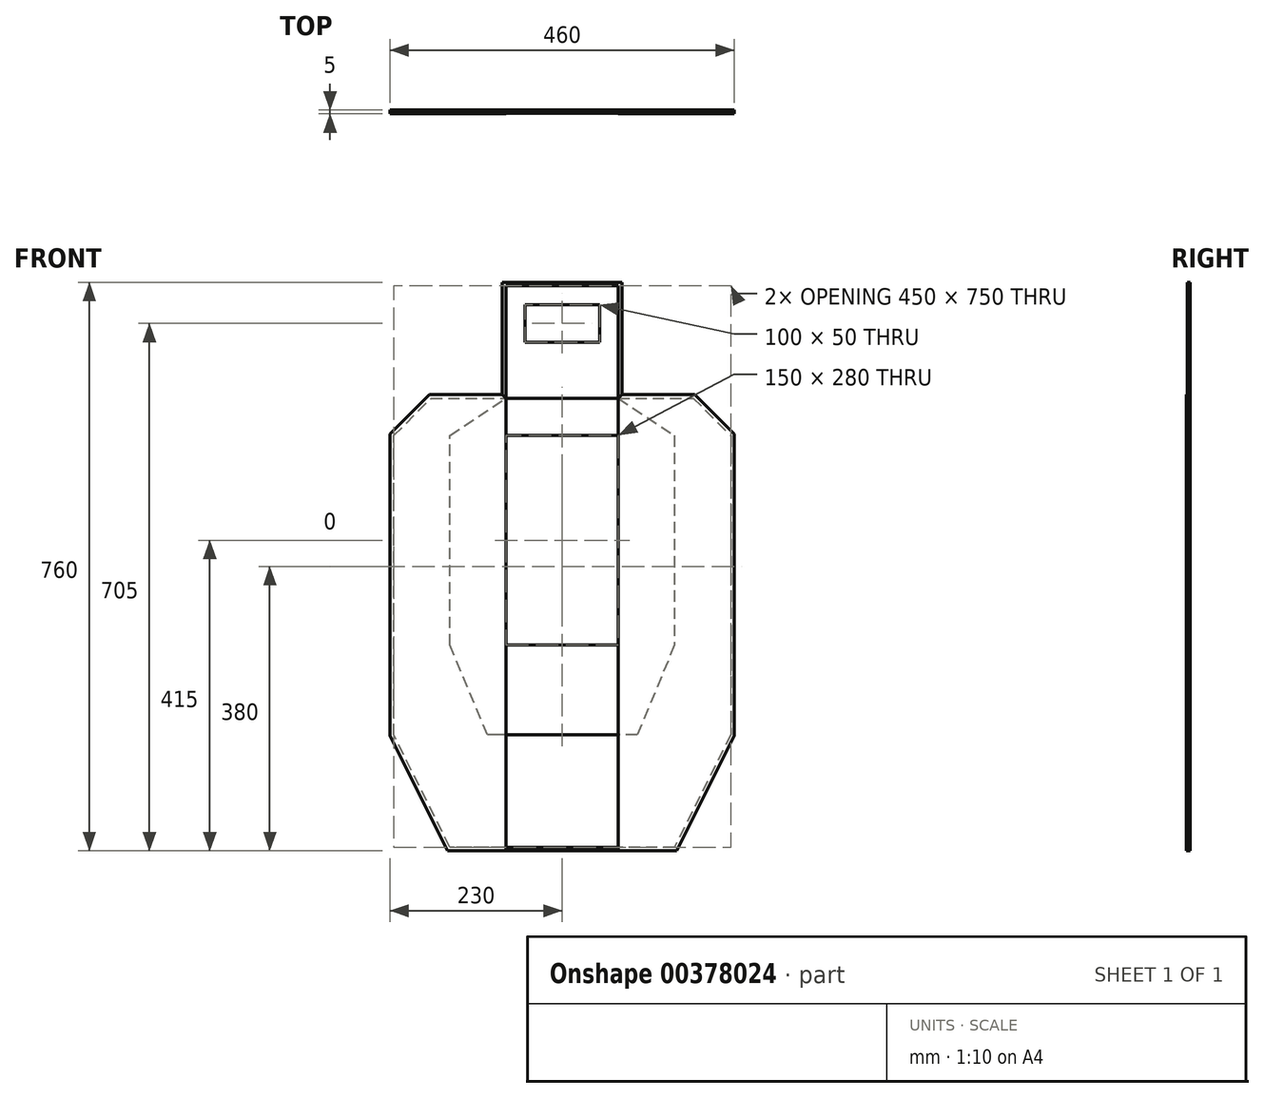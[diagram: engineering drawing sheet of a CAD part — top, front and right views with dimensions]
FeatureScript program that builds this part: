
annotation { "Feature Type Name" : "Feature", "Feature Type Description" : "" }
export const myFeature = defineFeature(function(context is Context, id is Id, definition is map)
    precondition{}
    {
        {
            var Q0;
            Q0=qCreatedBy(makeId("Front.planeOp"),FACE);
            var sketch = newSketch(context, id + "F0", { "sketchPlane" : qUnion([Q0])});
            skLineSegment(sketch, "E0.bottom", {"start": v(0, 100) * mm, "end": v(50, 100) * mm, "construction": true});
            skLineSegment(sketch, "E0.top", {"start": v(0, 125) * mm, "end": v(50, 125) * mm});
            skLineSegment(sketch, "E0.right", {"start": v(50, 100) * mm, "end": v(50, 125) * mm});
            skLineSegment(sketch, "E1.MirrorCS", {"start": v(0, 75) * mm, "end": v(50, 75) * mm});
            skLineSegment(sketch, "E2.MirrorCS", {"start": v(50, 100) * mm, "end": v(50, 75) * mm});
            skLineSegment(sketch, "E3.MirrorCS", {"start": v(0, 0) * mm, "end": v(0, 100) * mm, "construction": true});
            skLineSegment(sketch, "E4.MirrorCS", {"start": v(0, 125) * mm, "end": v(-50, 125) * mm});
            skLineSegment(sketch, "E5.MirrorCS", {"start": v(-50, 100) * mm, "end": v(-50, 125) * mm});
            skLineSegment(sketch, "E6.MirrorCS", {"start": v(-50, 100) * mm, "end": v(-50, 75) * mm});
            skLineSegment(sketch, "E7.MirrorCS", {"start": v(0, 75) * mm, "end": v(-50, 75) * mm});
            skSolve(sketch);
        }
        {
            var Q0;
            Q0=qSketchRegion(id+"F0",true);
            extrude(context, id + "F1", {"entities" : qUnion([Q0]), "oppositeDirection" : true, "depth" : 3 * mm});
        }
        {
            var Q0;
            Q0=qCreatedBy(makeId("Front.planeOp"),FACE);
            var sketch = newSketch(context, id + "F2", { "sketchPlane" : qUnion([Q0])});
            skLineSegment(sketch, "E8", {"start": v(75, 0) * mm, "end": v(75, 150) * mm});
            skLineSegment(sketch, "E9", {"start": v(75, 150) * mm, "end": v(-75, 150) * mm});
            skLineSegment(sketch, "E10", {"start": v(-75, 150) * mm, "end": v(-75, 0) * mm});
            skLineSegment(sketch, "E11", {"start": v(-75, 0) * mm, "end": v(75, 0) * mm});
            skLineSegment(sketch, "E12.0", {"start": v(0, 125) * mm, "end": v(-50, 125) * mm});
            skLineSegment(sketch, "E13.0", {"start": v(0, 125) * mm, "end": v(50, 125) * mm});
            skLineSegment(sketch, "E14.0", {"start": v(50, 100) * mm, "end": v(50, 125) * mm});
            skLineSegment(sketch, "E15.1", {"start": v(50, 100) * mm, "end": v(50, 75) * mm});
            skLineSegment(sketch, "E16.0", {"start": v(0, 75) * mm, "end": v(50, 75) * mm});
            skLineSegment(sketch, "E17.0", {"start": v(0, 75) * mm, "end": v(-50, 75) * mm});
            skLineSegment(sketch, "E18.0", {"start": v(-50, 100) * mm, "end": v(-50, 75) * mm});
            skLineSegment(sketch, "E19.1", {"start": v(-50, 100) * mm, "end": v(-50, 125) * mm});
            skLineSegment(sketch, "E20", {"start": v(0, 125) * mm, "end": v(0, 150) * mm, "construction": true});
            skLineSegment(sketch, "E21", {"start": v(0, 150) * mm, "end": v(0, 137.5) * mm, "construction": true});
            skSolve(sketch);
        }
        {
            var Q0;
            {var subQ0=sQuery(id+"F2.wireOp",EDGE,"E8");Q0=makeQuery(id+"F2.imprint","IMPRINT",FACE,{"disambiguationData":[TD([[makeQuery(id+"F2.imprint","IMPRINT",EDGE,{"derivedFrom":subQ0}),1.0]])]});}
            extrude(context, id + "F3", {"entities" : qUnion([Q0]), "oppositeDirection" : true, "depth" : 3 * mm});
        }
        {
            var Q0;
            Q0=qCreatedBy(makeId("Front.planeOp"),FACE);
            var sketch = newSketch(context, id + "F4", { "sketchPlane" : qUnion([Q0])});
            skLineSegment(sketch, "E22.bottom", {"start": v(75, -50) * mm, "end": v(-75, -50) * mm});
            skLineSegment(sketch, "E22.top", {"start": v(75, -330) * mm, "end": v(-75, -330) * mm});
            skLineSegment(sketch, "E22.left", {"start": v(75, -50) * mm, "end": v(75, -330) * mm});
            skLineSegment(sketch, "E22.right", {"start": v(-75, -50) * mm, "end": v(-75, -330) * mm});
            skLineSegment(sketch, "E23", {"start": v(0, 0) * mm, "end": v(0, -50) * mm, "construction": true});
            skLineSegment(sketch, "E24.0", {"start": v(-75, 0) * mm, "end": v(75, 0) * mm, "construction": true});
            skLineSegment(sketch, "E25", {"start": v(75, 0) * mm, "end": v(75, -50) * mm, "construction": true});
            skSolve(sketch);
        }
        {
            var Q0;
            Q0=makeQuery(id+"F4.imprint","IMPRINT",FACE,{"disambiguationData":[TD([[makeQuery(id+"F4.imprint","IMPRINT",EDGE,{"derivedFrom":sQuery(id+"F4.wireOp",EDGE,"E22.bottom")}),1.0]])]});
            extrude(context, id + "F5", {"entities" : qUnion([Q0]), "oppositeDirection" : true, "depth" : 3 * mm});
        }
        {
            var Q0;
            Q0=qCreatedBy(makeId("Front.planeOp"),FACE);
            var sketch = newSketch(context, id + "F6", { "sketchPlane" : qUnion([Q0])});
            skLineSegment(sketch, "E26.0", {"start": v(-75, 0) * mm, "end": v(75, 0) * mm});
            skLineSegment(sketch, "E27.1", {"start": v(75, -50) * mm, "end": v(75, -330) * mm});
            skLineSegment(sketch, "E28.2", {"start": v(75, -50) * mm, "end": v(-75, -50) * mm});
            skLineSegment(sketch, "E29.3", {"start": v(-75, -50) * mm, "end": v(-75, -330) * mm});
            skLineSegment(sketch, "E30.0", {"start": v(75, -330) * mm, "end": v(-75, -330) * mm});
            skLineSegment(sketch, "E31", {"start": v(75, 0) * mm, "end": v(150, -50) * mm});
            skLineSegment(sketch, "E32", {"start": v(150, -50) * mm, "end": v(150, -330) * mm});
            skLineSegment(sketch, "E33", {"start": v(150, -330) * mm, "end": v(100, -450) * mm});
            skLineSegment(sketch, "E34", {"start": v(100, -450) * mm, "end": v(-100, -450) * mm});
            skLineSegment(sketch, "E35", {"start": v(-100, -450) * mm, "end": v(-150, -330) * mm});
            skLineSegment(sketch, "E36", {"start": v(-150, -330) * mm, "end": v(-150, -50) * mm});
            skLineSegment(sketch, "E37", {"start": v(-150, -50) * mm, "end": v(-75, 0) * mm});
            skLineSegment(sketch, "E38", {"start": v(0, -450) * mm, "end": v(0, -50) * mm, "construction": true});
            skLineSegment(sketch, "E39", {"start": v(150, -50) * mm, "end": v(75, -50) * mm, "construction": true});
            skLineSegment(sketch, "E40", {"start": v(-55.04, -50) * mm, "end": v(-150, -50) * mm, "construction": true});
            skLineSegment(sketch, "E41", {"start": v(150, -330) * mm, "end": v(150, -450) * mm, "construction": true});
            skLineSegment(sketch, "E42", {"start": v(100, -450) * mm, "end": v(150, -450) * mm, "construction": true});
            skLineSegment(sketch, "E43", {"start": v(150, -330) * mm, "end": v(-150, -330) * mm, "construction": true});
            skLineSegment(sketch, "E44", {"start": v(-150, -330) * mm, "end": v(-150, -450) * mm, "construction": true});
            skLineSegment(sketch, "E45", {"start": v(-150, -450) * mm, "end": v(-100, -450) * mm, "construction": true});
            skSolve(sketch);
        }
        {
            var Q0;
            Q0=makeQuery(id+"F6.imprint","IMPRINT",FACE,{"disambiguationData":[TD([[makeQuery(id+"F6.imprint","IMPRINT",EDGE,{"derivedFrom":sQuery(id+"F6.wireOp",EDGE,"E26.0")}),-1.0]])]});
            extrude(context, id + "F7", {"entities" : qUnion([Q0]), "oppositeDirection" : true, "depth" : 3 * mm});
        }
        {
            var Q0;
            Q0=makeQuery(id+"F7.opExtrude","CAP_FACE",FACE,{"disambiguationData":[OSD([sQuery(id+"F6.wireOp",EDGE,"E26.0"),sQuery(id+"F6.wireOp",EDGE,"E27.1"),sQuery(id+"F6.wireOp",EDGE,"E28.2"),sQuery(id+"F6.wireOp",EDGE,"E29.3"),sQuery(id+"F6.wireOp",EDGE,"E30.0"),sQuery(id+"F6.wireOp",EDGE,"E31"),sQuery(id+"F6.wireOp",EDGE,"E32"),sQuery(id+"F6.wireOp",EDGE,"E33"),sQuery(id+"F6.wireOp",EDGE,"E34"),sQuery(id+"F6.wireOp",EDGE,"E35"),sQuery(id+"F6.wireOp",EDGE,"E36"),sQuery(id+"F6.wireOp",EDGE,"E37")])],"isStart":true});
            var sketch = newSketch(context, id + "F8", { "sketchPlane" : qUnion([Q0])});
            skLineSegment(sketch, "E46.0", {"start": v(75, 0) * mm, "end": v(150, -50) * mm});
            skLineSegment(sketch, "E47.0", {"start": v(150, -50) * mm, "end": v(150, -330) * mm});
            skLineSegment(sketch, "E48.0", {"start": v(150, -330) * mm, "end": v(100, -450) * mm});
            skLineSegment(sketch, "E49.1", {"start": v(100, -450) * mm, "end": v(-100, -450) * mm});
            skLineSegment(sketch, "E50.0", {"start": v(-150, -330) * mm, "end": v(-150, -50) * mm});
            skLineSegment(sketch, "E51.0", {"start": v(-100, -450) * mm, "end": v(-150, -330) * mm});
            skLineSegment(sketch, "E52.0", {"start": v(-150, -50) * mm, "end": v(-75, 0) * mm});
            skLineSegment(sketch, "E53", {"start": v(75, 0) * mm, "end": v(175, 0) * mm});
            skLineSegment(sketch, "E54", {"start": v(175, 0) * mm, "end": v(225, -50) * mm});
            skLineSegment(sketch, "E55", {"start": v(225, -50) * mm, "end": v(225, -450) * mm});
            skLineSegment(sketch, "E56", {"start": v(225, -450) * mm, "end": v(150, -600) * mm});
            skLineSegment(sketch, "E57", {"start": v(150, -600) * mm, "end": v(-150, -600) * mm});
            skLineSegment(sketch, "E58", {"start": v(-150, -600) * mm, "end": v(-225, -450) * mm});
            skLineSegment(sketch, "E59", {"start": v(-225, -450) * mm, "end": v(-225, -50) * mm});
            skLineSegment(sketch, "E60", {"start": v(-225, -50) * mm, "end": v(-175, 0) * mm});
            skLineSegment(sketch, "E61", {"start": v(-175, 0) * mm, "end": v(-75, 0) * mm});
            skLineSegment(sketch, "E62", {"start": v(225, -50) * mm, "end": v(225, 0) * mm, "construction": true});
            skLineSegment(sketch, "E63", {"start": v(225, 0) * mm, "end": v(175, 0) * mm, "construction": true});
            skLineSegment(sketch, "E64", {"start": v(225, -450) * mm, "end": v(225, -600) * mm, "construction": true});
            skLineSegment(sketch, "E65", {"start": v(225, -600) * mm, "end": v(150, -600) * mm, "construction": true});
            skLineSegment(sketch, "E66", {"start": v(-225, -450) * mm, "end": v(-225, -600) * mm, "construction": true});
            skLineSegment(sketch, "E67", {"start": v(-225, -600) * mm, "end": v(-150, -600) * mm, "construction": true});
            skLineSegment(sketch, "E68", {"start": v(-175, 0) * mm, "end": v(-225, 0) * mm, "construction": true});
            skLineSegment(sketch, "E69", {"start": v(-225, 0) * mm, "end": v(-225, -50) * mm, "construction": true});
            skSolve(sketch);
        }
        {
            var Q0;
            Q0=qSketchRegion(id+"F8",true);
            extrude(context, id + "F9", {"entities" : qUnion([Q0]), "oppositeDirection" : true, "depth" : 3 * mm});
        }
        {
            var Q0;
            Q0=makeQuery(id+"F9.opExtrude","CAP_FACE",FACE,{"disambiguationData":[OSD([sQuery(id+"F8.wireOp",EDGE,"E46.0"),sQuery(id+"F8.wireOp",EDGE,"E47.0"),sQuery(id+"F8.wireOp",EDGE,"E48.0"),sQuery(id+"F8.wireOp",EDGE,"E49.1"),sQuery(id+"F8.wireOp",EDGE,"E50.0"),sQuery(id+"F8.wireOp",EDGE,"E51.0"),sQuery(id+"F8.wireOp",EDGE,"E52.0"),sQuery(id+"F8.wireOp",EDGE,"E53"),sQuery(id+"F8.wireOp",EDGE,"E54"),sQuery(id+"F8.wireOp",EDGE,"E55"),sQuery(id+"F8.wireOp",EDGE,"E56"),sQuery(id+"F8.wireOp",EDGE,"E57"),sQuery(id+"F8.wireOp",EDGE,"E58"),sQuery(id+"F8.wireOp",EDGE,"E59"),sQuery(id+"F8.wireOp",EDGE,"E60"),sQuery(id+"F8.wireOp",EDGE,"E61")])],"isStart":true});
            var sketch = newSketch(context, id + "F10", { "sketchPlane" : qUnion([Q0])});
            skLineSegment(sketch, "E70.0", {"start": v(75, 150) * mm, "end": v(-75, 150) * mm});
            skLineSegment(sketch, "E71.0", {"start": v(75, 0) * mm, "end": v(75, 150) * mm});
            skLineSegment(sketch, "E72.1", {"start": v(75, 0) * mm, "end": v(175, 0) * mm});
            skLineSegment(sketch, "E73.0", {"start": v(175, 0) * mm, "end": v(225, -50) * mm});
            skLineSegment(sketch, "E74.1", {"start": v(225, -50) * mm, "end": v(225, -450) * mm});
            skLineSegment(sketch, "E75.0", {"start": v(225, -450) * mm, "end": v(150, -600) * mm});
            skLineSegment(sketch, "E76.1", {"start": v(150, -600) * mm, "end": v(-150, -600) * mm});
            skLineSegment(sketch, "E77.2", {"start": v(-150, -600) * mm, "end": v(-225, -450) * mm});
            skLineSegment(sketch, "E78.3", {"start": v(-225, -450) * mm, "end": v(-225, -50) * mm});
            skLineSegment(sketch, "E79.4", {"start": v(-225, -50) * mm, "end": v(-175, 0) * mm});
            skLineSegment(sketch, "E80.5", {"start": v(-175, 0) * mm, "end": v(-75, 0) * mm});
            skLineSegment(sketch, "E81.0", {"start": v(-75, 150) * mm, "end": v(-75, 0) * mm});
            skLineSegment(sketch, "E82.0", {"start": v(177.07, 5) * mm, "end": v(230, -47.93) * mm});
            skLineSegment(sketch, "E82.1", {"start": v(-230, -451.18) * mm, "end": v(-230, -47.93) * mm});
            skLineSegment(sketch, "E82.2", {"start": v(-153.1, -605) * mm, "end": v(-230, -451.18) * mm});
            skLineSegment(sketch, "E82.3", {"start": v(153.1, -605) * mm, "end": v(-153.1, -605) * mm});
            skLineSegment(sketch, "E82.4", {"start": v(230, -451.18) * mm, "end": v(153.1, -605) * mm});
            skLineSegment(sketch, "E82.5", {"start": v(-230, -47.93) * mm, "end": v(-177.07, 5) * mm});
            skLineSegment(sketch, "E82.6", {"start": v(230, -47.93) * mm, "end": v(230, -451.18) * mm});
            skLineSegment(sketch, "E82.7", {"start": v(-177.07, 5) * mm, "end": v(-80, 5) * mm});
            skLineSegment(sketch, "E82.8", {"start": v(-80, 155) * mm, "end": v(-80, 5) * mm});
            skLineSegment(sketch, "E82.9", {"start": v(80, 155) * mm, "end": v(-80, 155) * mm});
            skLineSegment(sketch, "E82.10", {"start": v(80, 5) * mm, "end": v(80, 155) * mm});
            skLineSegment(sketch, "E82.11", {"start": v(80, 5) * mm, "end": v(177.07, 5) * mm});
            skSolve(sketch);
        }
        {
            var Q0;
            Q0=makeQuery(id+"F10.imprint","IMPRINT",FACE,{"disambiguationData":[TD([[makeQuery(id+"F10.imprint","IMPRINT",EDGE,{"derivedFrom":sQuery(id+"F10.wireOp",EDGE,"E70.0")}),-1.0]])]});
            extrude(context, id + "F11", {"entities" : qUnion([Q0]), "oppositeDirection" : true, "depth" : 3 * mm});
        }
        {
            var Q0;
            Q0=makeQuery(id+"F9.opExtrude","CAP_FACE",FACE,{"disambiguationData":[OSD([sQuery(id+"F8.wireOp",EDGE,"E46.0"),sQuery(id+"F8.wireOp",EDGE,"E47.0"),sQuery(id+"F8.wireOp",EDGE,"E48.0"),sQuery(id+"F8.wireOp",EDGE,"E49.1"),sQuery(id+"F8.wireOp",EDGE,"E50.0"),sQuery(id+"F8.wireOp",EDGE,"E51.0"),sQuery(id+"F8.wireOp",EDGE,"E52.0"),sQuery(id+"F8.wireOp",EDGE,"E53"),sQuery(id+"F8.wireOp",EDGE,"E54"),sQuery(id+"F8.wireOp",EDGE,"E55"),sQuery(id+"F8.wireOp",EDGE,"E56"),sQuery(id+"F8.wireOp",EDGE,"E57"),sQuery(id+"F8.wireOp",EDGE,"E58"),sQuery(id+"F8.wireOp",EDGE,"E59"),sQuery(id+"F8.wireOp",EDGE,"E60"),sQuery(id+"F8.wireOp",EDGE,"E61")])],"isStart":false});
            var sketch = newSketch(context, id + "F12", { "sketchPlane" : qUnion([Q0])});
            skLineSegment(sketch, "E83.0", {"start": v(75, 150) * mm, "end": v(75, 0) * mm});
            skLineSegment(sketch, "E84.0", {"start": v(175, 0) * mm, "end": v(75, 0) * mm});
            skLineSegment(sketch, "E85.0", {"start": v(-75, 150) * mm, "end": v(75, 150) * mm});
            skLineSegment(sketch, "E86.0", {"start": v(225, -50) * mm, "end": v(175, 0) * mm});
            skLineSegment(sketch, "E87.0", {"start": v(-225, -50) * mm, "end": v(-225, -450) * mm});
            skLineSegment(sketch, "E87.1", {"start": v(225, -450) * mm, "end": v(225, -50) * mm});
            skLineSegment(sketch, "E87.2", {"start": v(150, -600) * mm, "end": v(225, -450) * mm});
            skLineSegment(sketch, "E87.3", {"start": v(-225, -450) * mm, "end": v(-150, -600) * mm});
            skLineSegment(sketch, "E87.4", {"start": v(-150, -600) * mm, "end": v(150, -600) * mm});
            skLineSegment(sketch, "E88.0", {"start": v(-175, 0) * mm, "end": v(-225, -50) * mm});
            skLineSegment(sketch, "E89.0", {"start": v(-75, 0) * mm, "end": v(-175, 0) * mm});
            skLineSegment(sketch, "E90.0", {"start": v(-75, 0) * mm, "end": v(-75, 150) * mm});
            skSolve(sketch);
        }
        {
            var Q0;
            Q0=qSketchRegion(id+"F12",true);
            extrude(context, id + "F13", {"entities" : qUnion([Q0]), "depth" : 1 * mm});
        }
        {
            var Q0;
            Q0=makeQuery(id+"F13.opExtrude","CAP_FACE",FACE,{"disambiguationData":[OSD([sQuery(id+"F12.wireOp",EDGE,"E83.0"),sQuery(id+"F12.wireOp",EDGE,"E84.0"),sQuery(id+"F12.wireOp",EDGE,"E85.0"),sQuery(id+"F12.wireOp",EDGE,"E86.0"),sQuery(id+"F12.wireOp",EDGE,"E87.0"),sQuery(id+"F12.wireOp",EDGE,"E87.1"),sQuery(id+"F12.wireOp",EDGE,"E87.2"),sQuery(id+"F12.wireOp",EDGE,"E87.3"),sQuery(id+"F12.wireOp",EDGE,"E87.4"),sQuery(id+"F12.wireOp",EDGE,"E88.0"),sQuery(id+"F12.wireOp",EDGE,"E89.0"),sQuery(id+"F12.wireOp",EDGE,"E90.0")])],"isStart":false});
            var sketch = newSketch(context, id + "F14", { "sketchPlane" : qUnion([Q0])});
            skLineSegment(sketch, "E91.0", {"start": v(-80, 155) * mm, "end": v(80, 155) * mm});
            skLineSegment(sketch, "E92.0", {"start": v(80, 155) * mm, "end": v(80, 5) * mm});
            skLineSegment(sketch, "E93.0", {"start": v(-80, 5) * mm, "end": v(-80, 155) * mm});
            skLineSegment(sketch, "E94.0", {"start": v(177.07, 5) * mm, "end": v(80, 5) * mm});
            skLineSegment(sketch, "E95.0", {"start": v(-80, 5) * mm, "end": v(-177.07, 5) * mm});
            skLineSegment(sketch, "E96.0", {"start": v(230, -47.93) * mm, "end": v(177.07, 5) * mm});
            skLineSegment(sketch, "E97.0", {"start": v(-177.07, 5) * mm, "end": v(-230, -47.93) * mm});
            skLineSegment(sketch, "E98.1", {"start": v(-230, -47.93) * mm, "end": v(-230, -451.18) * mm});
            skLineSegment(sketch, "E99.0", {"start": v(-230, -451.18) * mm, "end": v(-153.1, -605) * mm});
            skLineSegment(sketch, "E100.0", {"start": v(-153.1, -605) * mm, "end": v(153.1, -605) * mm});
            skLineSegment(sketch, "E101.0", {"start": v(153.1, -605) * mm, "end": v(230, -451.18) * mm});
            skLineSegment(sketch, "E102.0", {"start": v(230, -451.18) * mm, "end": v(230, -47.93) * mm});
            skLineSegment(sketch, "E103.0", {"start": v(-75, 150) * mm, "end": v(75, 150) * mm});
            skLineSegment(sketch, "E104.0", {"start": v(-75, 0) * mm, "end": v(-75, 150) * mm});
            skLineSegment(sketch, "E105.0", {"start": v(75, 150) * mm, "end": v(75, 0) * mm});
            skLineSegment(sketch, "E106.0", {"start": v(175, 0) * mm, "end": v(75, 0) * mm});
            skLineSegment(sketch, "E107.0", {"start": v(225, -50) * mm, "end": v(175, 0) * mm});
            skLineSegment(sketch, "E108.0", {"start": v(150, -600) * mm, "end": v(225, -450) * mm});
            skLineSegment(sketch, "E109.0", {"start": v(225, -450) * mm, "end": v(225, -50) * mm});
            skLineSegment(sketch, "E110.0", {"start": v(-150, -600) * mm, "end": v(150, -600) * mm});
            skLineSegment(sketch, "E111.0", {"start": v(-225, -450) * mm, "end": v(-150, -600) * mm});
            skLineSegment(sketch, "E112.0", {"start": v(-225, -50) * mm, "end": v(-225, -450) * mm});
            skLineSegment(sketch, "E113.0", {"start": v(-175, 0) * mm, "end": v(-225, -50) * mm});
            skLineSegment(sketch, "E114.0", {"start": v(-75, 0) * mm, "end": v(-175, 0) * mm});
            skSolve(sketch);
        }
        {
            var Q0;
            Q0=makeQuery(id+"F14.imprint","IMPRINT",FACE,{"disambiguationData":[TD([[makeQuery(id+"F14.imprint","IMPRINT",EDGE,{"derivedFrom":sQuery(id+"F14.wireOp",EDGE,"E91.0")}),-1.0]])]});
            extrude(context, id + "F15", {"entities" : qUnion([Q0]), "oppositeDirection" : true, "depth" : 1 * mm});
        }
        {
            var Q0;
            Q0=makeQuery(id+"F9.opExtrude","CAP_FACE",FACE,{"disambiguationData":[OSD([sQuery(id+"F8.wireOp",EDGE,"E46.0"),sQuery(id+"F8.wireOp",EDGE,"E47.0"),sQuery(id+"F8.wireOp",EDGE,"E48.0"),sQuery(id+"F8.wireOp",EDGE,"E49.1"),sQuery(id+"F8.wireOp",EDGE,"E50.0"),sQuery(id+"F8.wireOp",EDGE,"E51.0"),sQuery(id+"F8.wireOp",EDGE,"E52.0"),sQuery(id+"F8.wireOp",EDGE,"E53"),sQuery(id+"F8.wireOp",EDGE,"E54"),sQuery(id+"F8.wireOp",EDGE,"E55"),sQuery(id+"F8.wireOp",EDGE,"E56"),sQuery(id+"F8.wireOp",EDGE,"E57"),sQuery(id+"F8.wireOp",EDGE,"E58"),sQuery(id+"F8.wireOp",EDGE,"E59"),sQuery(id+"F8.wireOp",EDGE,"E60"),sQuery(id+"F8.wireOp",EDGE,"E61")])],"isStart":true});
            var sketch = newSketch(context, id + "F16", { "sketchPlane" : qUnion([Q0])});
            skLineSegment(sketch, "E115.0", {"start": v(-75, -605) * mm, "end": v(-153.1, -605) * mm});
            skLineSegment(sketch, "E116.0", {"start": v(-153.1, -605) * mm, "end": v(-230, -451.18) * mm});
            skLineSegment(sketch, "E117.0", {"start": v(-230, -451.18) * mm, "end": v(-230, -47.93) * mm});
            skLineSegment(sketch, "E118.0", {"start": v(-230, -47.93) * mm, "end": v(-177.07, 5) * mm});
            skLineSegment(sketch, "E119.0", {"start": v(-177.07, 5) * mm, "end": v(-80, 5) * mm});
            skLineSegment(sketch, "E120.0", {"start": v(-75, 0) * mm, "end": v(75, 0) * mm, "construction": true});
            skLineSegment(sketch, "E121", {"start": v(-80, 5) * mm, "end": v(-75, 0) * mm});
            skLineSegment(sketch, "E122", {"start": v(-75, 0) * mm, "end": v(-75, -605) * mm});
            skLineSegment(sketch, "E123", {"start": v(-75, -605) * mm, "end": v(-75, 0) * mm});
            skSolve(sketch);
        }
        {
            var Q0;
            Q0=qSketchRegion(id+"F16",true);
            extrude(context, id + "F17", {"entities" : qUnion([Q0]), "depth" : 1 * mm});
        }
        {
            var Q0;
            Q0=makeQuery(id+"F17.opExtrude","SWEPT_BODY",BODY,{"disambiguationData":[OSD([sQuery(id+"F16.wireOp",EDGE,"E115.0"),sQuery(id+"F16.wireOp",EDGE,"E116.0"),sQuery(id+"F16.wireOp",EDGE,"E117.0"),sQuery(id+"F16.wireOp",EDGE,"E118.0"),sQuery(id+"F16.wireOp",EDGE,"E119.0"),sQuery(id+"F16.wireOp",EDGE,"E121"),sQuery(id+"F16.wireOp",EDGE,"E123")])]});
            var Q1;
            Q1=qCreatedBy(makeId("Right.planeOp"),FACE);
            mirror(context, id + "F18", {"entities" : qUnion([Q0]), "mirrorPlane" : qUnion([Q1])});
        }
    });
